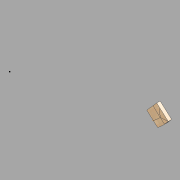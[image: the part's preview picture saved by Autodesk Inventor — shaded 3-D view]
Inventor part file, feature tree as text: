
AUTODESK INVENTOR PART (.ipt)
format: ipt  version: 2022.1 (Build 261234020, 234B)  size: 298,496 bytes
history: native  units: in
note: dims shown in document units (in); Inventor stores cm internally (conversion verified against a paired STEP export)
features: sketch x13, plane x5, extrude x5, other x3, projected_geometry x3, sweep x2
ambient origin geometry x8: Origin, YZ Plane, XZ Plane, XY Plane, X Axis, Y Axis, Z Axis, Center Point
bodies: Solid1 (feature_tree)
feature tree (31):
  other  "Wall_caps.ipt"
  plane  "Work Plane1"
  sketch  "Sketch1"  dims[d0=0.3937in d1=-6.125in]
  plane  "Work Plane2"
  sketch  "Sketch2"  dims[d2=-5.0in d3=3.0in]
  sketch  "Sketch3"  dims[d4=28.125in d5=0.0in d6=3.125in d7=0.0in]
  extrude  "Extrusion1"  [1 undecoded]
  extrude  "Extrusion2"  Depth=3.0in
  sketch  "Sketch6"  dims[d38=26.628in d39=0.0in d40=1.0in d41=0.0in]
  plane  "Work Plane4"
  extrude  "Extrusion8"  Depth=3.125in TaperAngle=0.0deg
  extrude  "Here"  Depth=0.25in
  sketch  "Sketch14"  dims[d46=0.0in d47=0.0in]
  extrude  "Extrusion10"  Depth=0.375in
  plane  "Work Plane5"
  sweep  "Sweep1"
  plane  "Work Plane6"
  sweep  "Sweep2"
  other  "Solid18::Wall_caps.ipt"
  other  "TaggingFeature1"
  sketch  "Sketch4"  dims[d15=135.0deg d35=0.25in]
  sketch  "Sketch5"  dims[d36=0.25in d37=0.375in]
  projected_geometry  "Projected Loop8"
  sketch  "Sketch12"  dims[d43=16.0in d44=63.0in]
  sketch  "Sketch13"  dims[d45=0.125in]
  sketch  "Sketch15"  dims[d48=0.125in]
  sketch  "Sketch16"  dims[d49=10.0in]
  sketch  "Sketch17"  dims[d50=0.125in]
  projected_geometry  "Projected Loop9"
  projected_geometry  "Projected Loop10"
  sketch  "Sketch19"  dims[d51=0.0in d52=0.0in d54=-6.125in d55=0.0in d56=0.0in]
note: 1 required parameter value undecoded (feature->parameter linkage not recoverable at this tier; creation-order binding heuristic only, values carry confidence <= 0.55)
